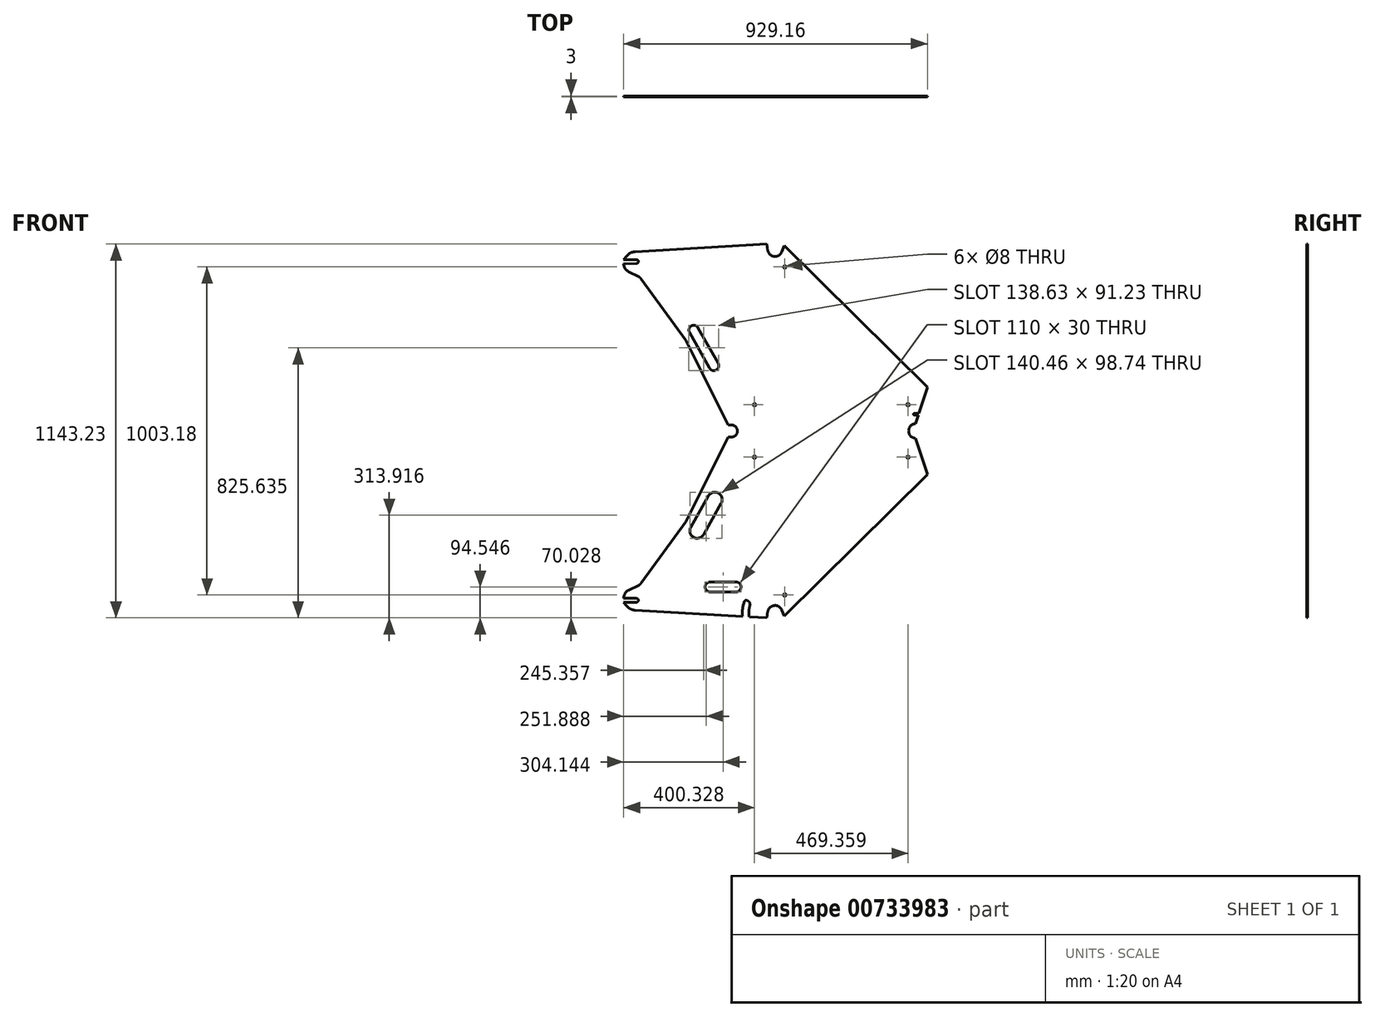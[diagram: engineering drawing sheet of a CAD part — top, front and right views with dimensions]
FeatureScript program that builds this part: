
annotation { "Feature Type Name" : "Feature", "Feature Type Description" : "" }
export const myFeature = defineFeature(function(context is Context, id is Id, definition is map)
    precondition{}
    {
        {
            var Q0;
            Q0=qCreatedBy(makeId("Front.planeOp"),FACE);
            var sketch = newSketch(context, id + "F0", { "sketchPlane" : qUnion([Q0])});
            skLineSegment(sketch, "E0", {"start": v(-160.76, 555.88) * mm, "end": v(408.24, 555.88) * mm, "construction": true});
            skLineSegment(sketch, "E1", {"start": v(408.24, 555.88) * mm, "end": v(445.83, 440.87) * mm, "construction": true});
            skArc(sketch, "E2", {"start": v(0.74, 26.27) * mm, "mid": v(-22.4, 40.64) * mm, "end": v(-42.43, 22.2) * mm});
            skLineSegment(sketch, "E3", {"start": v(-20.28, 18.24) * mm, "end": v(-144.86, 555.88) * mm, "construction": true});
            skLineSegment(sketch, "E4", {"start": v(-160.76, 555.88) * mm, "end": v(-39.05, 30.64) * mm, "construction": true});
            skLineSegment(sketch, "E5", {"start": v(-128.12, 555.88) * mm, "end": v(-7.89, 37.02) * mm, "construction": true});
            skLineSegment(sketch, "E6", {"start": v(0, 0) * mm, "end": v(-484.19, 28.1) * mm, "construction": true});
            skLineSegment(sketch, "E7", {"start": v(-160.76, 555.88) * mm, "end": v(-484.19, 28.1) * mm, "construction": true});
            skLineSegment(sketch, "E8", {"start": v(445.83, 440.87) * mm, "end": v(0, 0) * mm, "construction": true});
            skPoint(sketch, "E9", {"position": v(-176.43, 530.3) * mm});
            skPoint(sketch, "E10", {"position": v(-312.28, 308.61) * mm});
            skLineSegment(sketch, "E11", {"start": v(-312.28, 308.61) * mm, "end": v(-292.67, 296.6) * mm, "construction": true});
            skLineSegment(sketch, "E12", {"start": v(-176.43, 530.3) * mm, "end": v(-292.67, 296.6) * mm});
            skLineSegment(sketch, "E13", {"start": v(-429.8, 108.64) * mm, "end": v(-292.67, 296.6) * mm});
            skLineSegment(sketch, "E14", {"start": v(397.8, 555.88) * mm, "end": v(-163.71, 555.88) * mm});
            skLineSegment(sketch, "E15", {"start": v(409.57, 551.8) * mm, "end": v(445.83, 440.87) * mm});
            skLineSegment(sketch, "E16", {"start": v(445.83, 440.87) * mm, "end": v(7.82, 7.73) * mm});
            skPoint(sketch, "E17", {"position": v(-45.92, 2.66) * mm});
            skPoint(sketch, "E18", {"position": v(7.82, 7.73) * mm});
            skArc(sketch, "E19", {"start": v(7.82, 7.73) * mm, "mid": v(-23.1, 48.1) * mm, "end": v(-45.92, 2.66) * mm, "construction": true});
            skLineSegment(sketch, "E20", {"start": v(-176.43, 530.3) * mm, "end": v(-163.71, 555.88) * mm});
            skLineSegment(sketch, "E21", {"start": v(-173.75, 373) * mm, "end": v(-249.95, 238.03) * mm, "construction": true});
            skLineSegment(sketch, "E22", {"start": v(-186.81, 380.38) * mm, "end": v(-263, 245.4) * mm, "construction": true});
            skPoint(sketch, "E23.visualSharp", {"position": v(-289.13, 260.15) * mm});
            skPoint(sketch, "E24.visualSharp", {"position": v(-249.95, 238.03) * mm});
            skLineSegment(sketch, "E25", {"start": v(-212.94, 395.13) * mm, "end": v(-289.13, 260.15) * mm, "construction": true});
            skLineSegment(sketch, "E26", {"start": v(-249.95, 238.03) * mm, "end": v(-289.13, 260.15) * mm, "construction": true});
            skLineSegment(sketch, "E27", {"start": v(-212.94, 395.13) * mm, "end": v(-173.75, 373) * mm, "construction": true});
            skLineSegment(sketch, "E28", {"start": v(-292.67, 296.6) * mm, "end": v(-274.39, 286.27) * mm, "construction": true});
            skArc(sketch, "E29", {"start": v(-278.07, 279.74) * mm, "mid": v(-269.54, 249.09) * mm, "end": v(-238.88, 257.62) * mm});
            skLineSegment(sketch, "E30", {"start": v(-278.07, 279.74) * mm, "end": v(-238.88, 257.62) * mm, "construction": true});
            skArc(sketch, "E31", {"start": v(-184.81, 353.41) * mm, "mid": v(-193.34, 384.07) * mm, "end": v(-224, 375.53) * mm});
            skLineSegment(sketch, "E32", {"start": v(-224, 375.53) * mm, "end": v(-184.81, 353.41) * mm, "construction": true});
            skLineSegment(sketch, "E33", {"start": v(-278.07, 279.74) * mm, "end": v(-224, 375.53) * mm});
            skLineSegment(sketch, "E34", {"start": v(-184.81, 353.41) * mm, "end": v(-238.88, 257.62) * mm});
            skLineSegment(sketch, "E35.bottom", {"start": v(-234.19, 112.2) * mm, "end": v(-124.19, 112.2) * mm, "construction": true});
            skLineSegment(sketch, "E35.top", {"start": v(-234.19, 82.2) * mm, "end": v(-124.19, 82.2) * mm, "construction": true});
            skLineSegment(sketch, "E35.left", {"start": v(-234.19, 112.2) * mm, "end": v(-234.19, 82.2) * mm, "construction": true});
            skLineSegment(sketch, "E35.right", {"start": v(-124.19, 112.2) * mm, "end": v(-124.19, 82.2) * mm, "construction": true});
            skLineSegment(sketch, "E36", {"start": v(-124.19, 82.2) * mm, "end": v(-124.19, 7.2) * mm, "construction": true});
            skArc(sketch, "E37", {"start": v(-219.19, 112.2) * mm, "mid": v(-234.19, 97.2) * mm, "end": v(-219.19, 82.2) * mm});
            skArc(sketch, "E38", {"start": v(-139.19, 82.2) * mm, "mid": v(-124.19, 97.2) * mm, "end": v(-139.19, 112.2) * mm});
            skLineSegment(sketch, "E39", {"start": v(-139.19, 112.2) * mm, "end": v(-139.19, 82.2) * mm, "construction": true});
            skLineSegment(sketch, "E40", {"start": v(-219.19, 112.2) * mm, "end": v(-139.19, 112.2) * mm});
            skLineSegment(sketch, "E41", {"start": v(-139.19, 82.2) * mm, "end": v(-219.19, 82.2) * mm});
            skLineSegment(sketch, "E42", {"start": v(-641.86, 574.28) * mm, "end": v(862.04, 574.28) * mm, "construction": true});
            skLineSegment(sketch, "E43.MirrorCS", {"start": v(-312.28, 839.94) * mm, "end": v(-292.67, 851.96) * mm, "construction": true});
            skLineSegment(sketch, "E44.MirrorCS", {"start": v(-176.43, 618.26) * mm, "end": v(-163.71, 592.68) * mm});
            skLineSegment(sketch, "E45.MirrorCS", {"start": v(-249.95, 910.53) * mm, "end": v(-289.13, 888.41) * mm, "construction": true});
            skLineSegment(sketch, "E46.MirrorCS", {"start": v(-447.54, 1122.59) * mm, "end": v(-461.2, 1082.95) * mm, "construction": true});
            skLineSegment(sketch, "E47.MirrorCS", {"start": v(-212.94, 753.43) * mm, "end": v(-173.75, 775.55) * mm, "construction": true});
            skLineSegment(sketch, "E48.MirrorCS", {"start": v(-292.67, 851.96) * mm, "end": v(-274.39, 862.29) * mm, "construction": true});
            skLineSegment(sketch, "E49.MirrorCS", {"start": v(-45.92, 1145.9) * mm, "end": v(-447.54, 1122.59) * mm});
            skArc(sketch, "E50.MirrorC", {"start": v(0.74, 1122.29) * mm, "mid": v(-22.4, 1107.92) * mm, "end": v(-42.43, 1126.36) * mm});
            skLineSegment(sketch, "E51.MirrorCS", {"start": v(445.83, 707.7) * mm, "end": v(7.82, 1140.82) * mm});
            skLineSegment(sketch, "E52.MirrorCS", {"start": v(397.8, 592.68) * mm, "end": v(-163.71, 592.68) * mm});
            skLineSegment(sketch, "E53.MirrorCS", {"start": v(409.57, 596.75) * mm, "end": v(418.05, 622.68) * mm});
            skArc(sketch, "E54.MirrorCS", {"start": v(7.82, 1140.82) * mm, "mid": v(-23.1, 1100.45) * mm, "end": v(-45.92, 1145.9) * mm, "construction": true});
            skPoint(sketch, "E55.MirrorP", {"position": v(-289.13, 888.41) * mm});
            skLineSegment(sketch, "E56.MirrorCS", {"start": v(-20.28, 1130.32) * mm, "end": v(-144.86, 592.68) * mm, "construction": true});
            skPoint(sketch, "E57.MirrorP", {"position": v(-312.28, 839.94) * mm});
            skLineSegment(sketch, "E58.MirrorCS", {"start": v(-128.12, 592.68) * mm, "end": v(-7.89, 1111.54) * mm, "construction": true});
            skPoint(sketch, "E59.MirrorP", {"position": v(-176.43, 618.26) * mm});
            skPoint(sketch, "E60.MirrorP", {"position": v(-45.92, 1145.9) * mm});
            skLineSegment(sketch, "E61.MirrorCS", {"start": v(-160.76, 592.68) * mm, "end": v(397.8, 592.68) * mm, "construction": true});
            skPoint(sketch, "E62.MirrorP", {"position": v(7.82, 1140.82) * mm});
            skLineSegment(sketch, "E63.MirrorCS", {"start": v(-160.76, 592.68) * mm, "end": v(-39.05, 1117.92) * mm, "construction": true});
            skLineSegment(sketch, "E64.MirrorCS", {"start": v(-160.76, 592.68) * mm, "end": v(-484.19, 1120.46) * mm, "construction": true});
            skLineSegment(sketch, "E65.MirrorCS", {"start": v(-186.81, 768.18) * mm, "end": v(-263, 903.16) * mm, "construction": true});
            skPoint(sketch, "E66.MirrorP", {"position": v(-249.95, 910.53) * mm});
            skPoint(sketch, "E67.MirrorP", {"position": v(-461.2, 1082.95) * mm});
            skLineSegment(sketch, "E68.MirrorCS", {"start": v(445.83, 707.7) * mm, "end": v(0, 1148.56) * mm, "construction": true});
            skLineSegment(sketch, "E69.MirrorCS", {"start": v(409.57, 596.75) * mm, "end": v(418.05, 622.68) * mm, "construction": true});
            skLineSegment(sketch, "E70.MirrorCS", {"start": v(-461.2, 1082.95) * mm, "end": v(-292.67, 851.96) * mm});
            skLineSegment(sketch, "E71.MirrorCS", {"start": v(-176.43, 618.26) * mm, "end": v(-178.63, 622.68) * mm});
            skLineSegment(sketch, "E72.MirrorCS", {"start": v(0, 1148.56) * mm, "end": v(-484.19, 1120.46) * mm, "construction": true});
            skLineSegment(sketch, "E73", {"start": v(-255.63, 890.1) * mm, "end": v(-194.19, 781.24) * mm});
            skArc(sketch, "E74", {"start": v(-255.63, 890.1) * mm, "mid": v(-276.07, 895.78) * mm, "end": v(-281.76, 875.35) * mm});
            skLineSegment(sketch, "E75", {"start": v(-289.13, 888.41) * mm, "end": v(-212.94, 753.43) * mm, "construction": true});
            skLineSegment(sketch, "E76", {"start": v(-281.76, 875.35) * mm, "end": v(-255.63, 890.1) * mm, "construction": true});
            skArc(sketch, "E77", {"start": v(-220.31, 766.5) * mm, "mid": v(-199.88, 760.8) * mm, "end": v(-194.19, 781.24) * mm});
            skLineSegment(sketch, "E78", {"start": v(-220.31, 766.5) * mm, "end": v(-194.19, 781.24) * mm, "construction": true});
            skLineSegment(sketch, "E79", {"start": v(-281.76, 875.35) * mm, "end": v(-220.31, 766.5) * mm});
            skArc(sketch, "E80.trimOffspring", {"start": v(-153.71, 555.88) * mm, "mid": v(-135.31, 574.28) * mm, "end": v(-153.71, 592.68) * mm});
            skArc(sketch, "E81", {"start": v(409.57, 596.75) * mm, "mid": v(388.24, 574.28) * mm, "end": v(409.57, 551.8) * mm});
            skLineSegment(sketch, "E82", {"start": v(388.24, 592.68) * mm, "end": v(388.24, 555.88) * mm, "construction": true});
            skPoint(sketch, "E83.orphan", {"position": v(408.24, 592.68) * mm});
            skPoint(sketch, "E84.orphan", {"position": v(408.24, 555.88) * mm});
            skLineSegment(sketch, "E85", {"start": v(-437.04, 102.52) * mm, "end": v(-516.22, 63.05) * mm, "construction": true});
            skLineSegment(sketch, "E86", {"start": v(-516.22, 63.05) * mm, "end": v(-444.22, 62.36) * mm, "construction": true});
            skLineSegment(sketch, "E87", {"start": v(-438.28, 56.3) * mm, "end": v(-438.28, 56.3) * mm});
            skLineSegment(sketch, "E88", {"start": v(-444.33, 50.36) * mm, "end": v(-483.33, 50.74) * mm});
            skLineSegment(sketch, "E89", {"start": v(-483.33, 50.74) * mm, "end": v(-463.52, 26.9) * mm});
            skPoint(sketch, "E90.orphan", {"position": v(-439.25, 101.42) * mm});
            skPoint(sketch, "E91.end.orphan", {"position": v(-461.2, 65.61) * mm});
            skArc(sketch, "E92", {"start": v(-467.98, 87.1) * mm, "mid": v(-479.03, 77.06) * mm, "end": v(-483.22, 62.74) * mm});
            skLineSegment(sketch, "E93", {"start": v(-483.22, 62.74) * mm, "end": v(-482.71, 115.9) * mm, "construction": true});
            skPoint(sketch, "E94.visualSharp", {"position": v(-438.22, 62.3) * mm});
            skArc(sketch, "E94.filletArc", {"start": v(-438.28, 56.3) * mm, "mid": v(-440, 60.57) * mm, "end": v(-444.22, 62.36) * mm});
            skPoint(sketch, "E95.visualSharp", {"position": v(-438.33, 50.3) * mm});
            skArc(sketch, "E95.filletArc", {"start": v(-444.33, 50.36) * mm, "mid": v(-440.07, 52.08) * mm, "end": v(-438.28, 56.3) * mm});
            skLineSegment(sketch, "E96", {"start": v(-467.98, 87.1) * mm, "end": v(-437.04, 102.52) * mm, "construction": true});
            skLineSegment(sketch, "E97", {"start": v(-467.98, 87.1) * mm, "end": v(-437.04, 102.52) * mm});
            skLineSegment(sketch, "E98", {"start": v(-483.22, 62.74) * mm, "end": v(-444.22, 62.36) * mm});
            skLineSegment(sketch, "E99", {"start": v(-463.52, 26.9) * mm, "end": v(-447.54, 25.97) * mm, "construction": true});
            skArc(sketch, "E100", {"start": v(-473.74, 39.2) * mm, "mid": v(-462.02, 29.86) * mm, "end": v(-447.54, 25.97) * mm});
            skLineSegment(sketch, "E101", {"start": v(-483.22, 62.74) * mm, "end": v(-483.33, 50.74) * mm, "construction": true});
            skPoint(sketch, "E102.visualSharp", {"position": v(-432.68, 104.7) * mm});
            skArc(sketch, "E102.filletArc", {"start": v(-437.04, 102.52) * mm, "mid": v(-433.06, 105.15) * mm, "end": v(-429.8, 108.64) * mm});
            skLineSegment(sketch, "E103.MirrorCS", {"start": v(-467.98, 1061.46) * mm, "end": v(-437.04, 1046.03) * mm});
            skLineSegment(sketch, "E104.MirrorCS", {"start": v(-483.22, 1085.82) * mm, "end": v(-444.22, 1086.2) * mm});
            skArc(sketch, "E105.MirrorCS", {"start": v(-444.33, 1098.2) * mm, "mid": v(-440.07, 1096.48) * mm, "end": v(-438.28, 1092.25) * mm});
            skArc(sketch, "E106.MirrorCS", {"start": v(-438.28, 1092.25) * mm, "mid": v(-440, 1088) * mm, "end": v(-444.22, 1086.2) * mm});
            skArc(sketch, "E107.MirrorCS", {"start": v(-437.04, 1046.03) * mm, "mid": v(-433.06, 1043.41) * mm, "end": v(-429.8, 1039.92) * mm});
            skLineSegment(sketch, "E108.MirrorCS", {"start": v(-444.33, 1098.2) * mm, "end": v(-483.33, 1097.82) * mm});
            skLineSegment(sketch, "E109.MirrorCS", {"start": v(-463.52, 1121.66) * mm, "end": v(-447.54, 1122.59) * mm, "construction": true});
            skPoint(sketch, "E110.MirrorP", {"position": v(-438.22, 1086.25) * mm});
            skArc(sketch, "E111.MirrorCS", {"start": v(-473.74, 1109.36) * mm, "mid": v(-462.02, 1118.7) * mm, "end": v(-447.54, 1122.59) * mm});
            skLineSegment(sketch, "E112.MirrorCS", {"start": v(-516.22, 1085.5) * mm, "end": v(-444.22, 1086.2) * mm, "construction": true});
            skLineSegment(sketch, "E113.MirrorCS", {"start": v(-483.22, 1085.82) * mm, "end": v(-482.71, 1032.66) * mm, "construction": true});
            skArc(sketch, "E114.MirrorCS", {"start": v(-467.98, 1061.46) * mm, "mid": v(-479.03, 1071.5) * mm, "end": v(-483.22, 1085.82) * mm});
            skLineSegment(sketch, "E115.MirrorCS", {"start": v(-483.33, 1097.82) * mm, "end": v(-463.52, 1121.66) * mm});
            skPoint(sketch, "E116.MirrorP", {"position": v(-432.68, 1043.86) * mm});
            skPoint(sketch, "E117.MirrorP", {"position": v(-438.33, 1098.25) * mm});
            skLineSegment(sketch, "E118.MirrorCS", {"start": v(-467.98, 1061.46) * mm, "end": v(-437.04, 1046.03) * mm, "construction": true});
            skLineSegment(sketch, "E119.MirrorCS", {"start": v(-437.04, 1046.03) * mm, "end": v(-516.22, 1085.5) * mm, "construction": true});
            skLineSegment(sketch, "E120.MirrorCS", {"start": v(-483.22, 1085.82) * mm, "end": v(-483.33, 1097.82) * mm, "construction": true});
            skPoint(sketch, "E121.MirrorP", {"position": v(-439.25, 1047.14) * mm});
            skLineSegment(sketch, "E122", {"start": v(-91.14, 55.37) * mm, "end": v(-109, 56.4) * mm});
            skCircle(sketch, "E123", {"center": v(-20.28, 18.24) * mm, "radius": 100 * mm, "construction": true});
            skCircle(sketch, "E124", {"center": v(-20.28, 18.24) * mm, "radius": 80 * mm, "construction": true});
            skArc(sketch, "E125", {"start": v(-113.98, 53.16) * mm, "mid": v(-119.54, 30.39) * mm, "end": v(-119.64, 6.94) * mm});
            skArc(sketch, "E126", {"start": v(-91.14, 55.37) * mm, "mid": v(-99.22, 31.23) * mm, "end": v(-99.3, 5.76) * mm});
            skPoint(sketch, "E127.visualSharp", {"position": v(-112.62, 56.62) * mm});
            skArc(sketch, "E127.filletArc", {"start": v(-109, 56.4) * mm, "mid": v(-112.03, 55.6) * mm, "end": v(-113.98, 53.16) * mm});
            skLineSegment(sketch, "E128", {"start": v(-119.64, 6.94) * mm, "end": v(-447.54, 25.97) * mm});
            skLineSegment(sketch, "E129", {"start": v(-99.3, 5.76) * mm, "end": v(-45.92, 2.66) * mm});
            skCircle(sketch, "E130", {"center": v(-83, 654.48) * mm, "radius": 4 * mm});
            skCircle(sketch, "E131", {"center": v(386.36, 654.48) * mm, "radius": 4 * mm});
            skCircle(sketch, "E132", {"center": v(9.5, 1075.87) * mm, "radius": 4 * mm});
            skLineSegment(sketch, "E133", {"start": v(-120.75, 624.48) * mm, "end": v(418.63, 624.48) * mm, "construction": true});
            skLineSegment(sketch, "E134", {"start": v(437.88, 715.55) * mm, "end": v(397.7, 592.61) * mm, "construction": true});
            skLineSegment(sketch, "E135", {"start": v(0, 1108.22) * mm, "end": v(435.87, 677.2) * mm, "construction": true});
            skCircle(sketch, "E136.MirrorC", {"center": v(9.5, 72.69) * mm, "radius": 4 * mm});
            skCircle(sketch, "E137.MirrorC", {"center": v(-83, 494.08) * mm, "radius": 4 * mm});
            skCircle(sketch, "E138.MirrorC", {"center": v(386.36, 494.08) * mm, "radius": 4 * mm});
            skLineSegment(sketch, "E139", {"start": v(-153.71, 592.68) * mm, "end": v(-153.71, 555.88) * mm, "construction": true});
            skLineSegment(sketch, "E140", {"start": v(-42.43, 22.2) * mm, "end": v(-45.92, 2.66) * mm});
            skLineSegment(sketch, "E141", {"start": v(0.74, 26.27) * mm, "end": v(7.82, 7.73) * mm});
            skLineSegment(sketch, "E142", {"start": v(-45.92, 1145.9) * mm, "end": v(-42.43, 1126.36) * mm});
            skLineSegment(sketch, "E143", {"start": v(0.74, 1122.29) * mm, "end": v(7.82, 1140.82) * mm});
            skArc(sketch, "E144", {"start": v(-97.28, 39.95) * mm, "mid": v(-99.2, 50.99) * mm, "end": v(-109, 56.4) * mm});
            skLineSegment(sketch, "E145", {"start": v(-530.7, 62.82) * mm, "end": v(-438.1, 61.94) * mm, "construction": true});
            skLineSegment(sketch, "E146", {"start": v(-438.1, 61.94) * mm, "end": v(-438.2, 50.97) * mm, "construction": true});
            skLineSegment(sketch, "E147", {"start": v(-438.2, 50.97) * mm, "end": v(-529.63, 51.84) * mm, "construction": true});
            skLineSegment(sketch, "E148.trimOffspring", {"start": v(-178.63, 622.68) * mm, "end": v(-292.67, 851.96) * mm});
            skLineSegment(sketch, "E149", {"start": v(431.28, 622.68) * mm, "end": v(406.05, 622.68) * mm, "construction": true});
            skLineSegment(sketch, "E150", {"start": v(418.05, 622.68) * mm, "end": v(403.05, 622.68) * mm});
            skLineSegment(sketch, "E151", {"start": v(403.05, 625.68) * mm, "end": v(403.05, 625.68) * mm});
            skLineSegment(sketch, "E152", {"start": v(406.05, 628.68) * mm, "end": v(420, 628.68) * mm});
            skPoint(sketch, "E153.visualSharp", {"position": v(403.05, 628.68) * mm});
            skArc(sketch, "E153.filletArc", {"start": v(406.05, 628.68) * mm, "mid": v(403.92, 627.8) * mm, "end": v(403.05, 625.68) * mm});
            skPoint(sketch, "E154.newPointA", {"position": v(403.05, 622.68) * mm});
            skArc(sketch, "E154.filletArc", {"start": v(403.05, 625.68) * mm, "mid": v(403.92, 623.56) * mm, "end": v(406.05, 622.68) * mm});
            skLineSegment(sketch, "E155.trimOffspring", {"start": v(420, 628.68) * mm, "end": v(445.83, 707.7) * mm, "construction": true});
            skLineSegment(sketch, "E156.trimOffspring", {"start": v(420, 628.68) * mm, "end": v(445.83, 707.7) * mm});
            skSolve(sketch);
        }
        {
            var Q0;
            Q0 = qSketchRegion(id + "F0", true);
            extrude(context, id + "F1", {"entities" : qUnion([Q0]), "depth" : 3 * mm, "offsetDistance" : 25 * mm});
        }
    });
